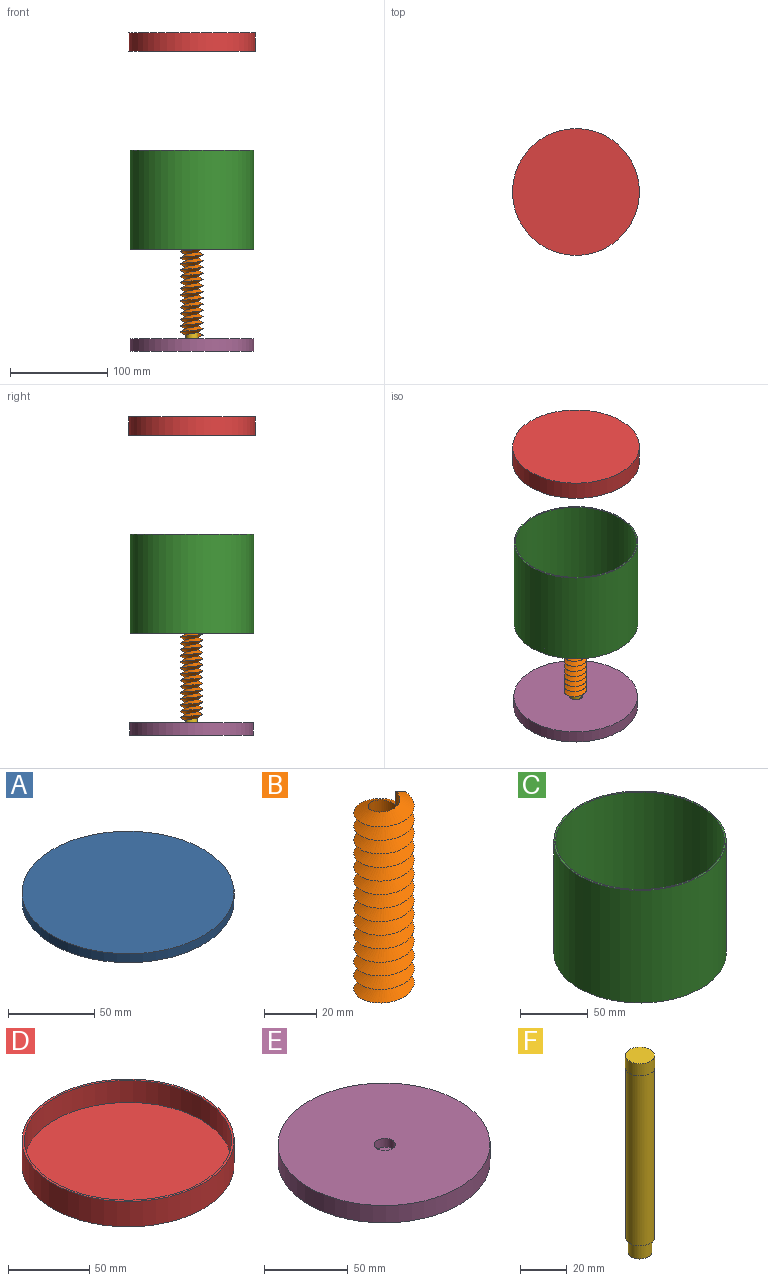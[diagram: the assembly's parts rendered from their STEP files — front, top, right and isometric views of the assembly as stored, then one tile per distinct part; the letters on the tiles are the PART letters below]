
ASSEMBLY  parts=6 mates=5
PART A: 5 faces, bbox 123.2x123.2x6.4 mm
  f0: cylinder r=61.59mm len=123.19mm, axis (0,0,-1), area 2457.5mm2, adj f1,f2
  f1: plane 123.19x123.19mm, normal (0,0,1), area 11919mm2, adj f0
  f2: plane 123.19x123.19mm, normal (0,0,-1), area 11838mm2, adj f0,f3
  f3: cylinder r=5.08mm len=10.16mm, axis (0,0,-1), area 162.1mm2, adj f2,f4
  f4: plane 10.16x10.16mm, normal (0,0,-1), area 81.1mm2, adj f3
PART B: 5 faces, bbox 23.1x26.7x95.2 mm
  f0: plane 6.3x5.46mm, normal (0,-1,0), area 17.2mm2, adj f2,f3,f4
  f1: plane 6.3x5.46mm, normal (0,1,0), area 17.2mm2, adj f2,f3,f4
  f2: cylinder r=6.1mm len=95.2mm, axis (0,0,1), area 3377.8mm2, adj f0,f1,f3,f4
  f3: bspline ~92.05x26.68mm, area 4944.1mm2, adj f0,f1,f2,f4
  f4: bspline ~92.05x26.68mm, area 4944.1mm2, adj f0,f1,f2,f3
PART C: 9 faces, bbox 127x127x105.8 mm
  f0: cylinder r=63.5mm len=127mm, axis (0,0,-1), area 40536.6mm2, adj f1,f2
  f1: plane 127x127mm, normal (0,0,1), area 501.6mm2, adj f0,f3
  f2: plane 127x127mm, normal (0,0,-1), area 12402.2mm2, adj f0,f5,f6,f7
  f3: cylinder r=62.23mm len=124.46mm, axis (0,0,1), area 37243mm2, adj f1,f4
  f4: plane 124.46x124.46mm, normal (0,0,1), area 12039.4mm2, adj f3,f5
  f5: cylinder r=6.35mm len=12.7mm, axis (0,0,-1), area 126.7mm2, adj f2,f4,f6,f7,f8
  f6: bspline ~27.26x23.61mm, area 262.6mm2, adj f2,f5,f7,f8
  f7: bspline ~23.86x23.61mm, area 101.3mm2, adj f2,f5,f6,f8
  f8: plane 6.3x5.46mm, normal (0,-1,0), area 17.2mm2, adj f5,f6,f7
PART D: 5 faces, bbox 130.2x130.2x19.1 mm
  f0: cylinder r=65.09mm len=130.18mm, axis (0,0,-1), area 7790.6mm2, adj f1,f2
  f1: plane 130.18x130.18mm, normal (0,0,1), area 590.6mm2, adj f0,f3
  f2: plane 130.18x130.18mm, normal (0,0,-1), area 13309mm2, adj f0
  f3: cylinder r=63.63mm len=127.25mm, axis (0,0,1), area 6600.4mm2, adj f1,f4
  f4: plane 127.25x127.25mm, normal (0,0,1), area 12718.4mm2, adj f3
PART E: 5 faces, bbox 127x127x12.7 mm
  f0: cylinder r=63.5mm len=127mm, axis (0,0,-1), area 5067.1mm2, adj f1,f2
  f1: plane 127x127mm, normal (0,0,1), area 12541mm2, adj f0,f3
  f2: plane 127x127mm, normal (0,0,-1), area 12667.7mm2, adj f0
  f3: cylinder r=6.35mm len=12.7mm, axis (0,0,1), area 253.4mm2, adj f1,f4
  f4: plane 12.7x12.7mm, normal (0,0,1), area 126.7mm2, adj f3
PART F: 7 faces, bbox 12.4x12.4x102.9 mm
  f0: cylinder r=6.1mm len=88.9mm, axis (0,0,-1), area 3405.1mm2, adj f1,f4
  f1: plane 12.19x12.19mm, normal (0,0,-1), area 39.7mm2, adj f0,f5
  f2: cylinder r=6.22mm len=12.45mm, axis (0,0,-1), area 248.3mm2, adj f3,f4
  f3: plane 12.45x12.45mm, normal (0,0,1), area 121.7mm2, adj f2
  f4: plane 12.45x12.45mm, normal (0,0,-1), area 4.9mm2, adj f0,f2
  f5: cylinder r=4.95mm len=9.91mm, axis (0,0,1), area 237.1mm2, adj f1,f6
  f6: plane 9.91x9.91mm, normal (0,0,-1), area 77.1mm2, adj f5
PLACE A t=(0.16,-0.78,106.05)mm
PLACE B rot(axis=(1,0,0),180deg) t=(0,0,102.17)mm
PLACE C t=(0.16,-0.47,104.71)mm
PLACE D rot(axis=(1,0,0),180deg) t=(0.16,-0.47,326.7)mm
PLACE E at identity
PLACE F rot(axis=(1,0,0),180deg) t=(0,0,101.6)mm
MATE fastened B.f2 <-> E.f0  axis (0,0,-1) through (0,0,12.7)mm
MATE slider D.f0 <-> C.f3  axis (0,0,1) through (0.16,-0.47,326.7)mm
MATE fastened F.f2 <-> E.f0  axis (0,0,1) through (0,0,6.35)mm
MATE slider E.f3 <-> C.f0  axis (0,0,1) through (0.16,-0.47,12.7)mm
MATE fastened F.f5 <-> A.f0  axis (0,0,1) through (0,0,109.22)mm
